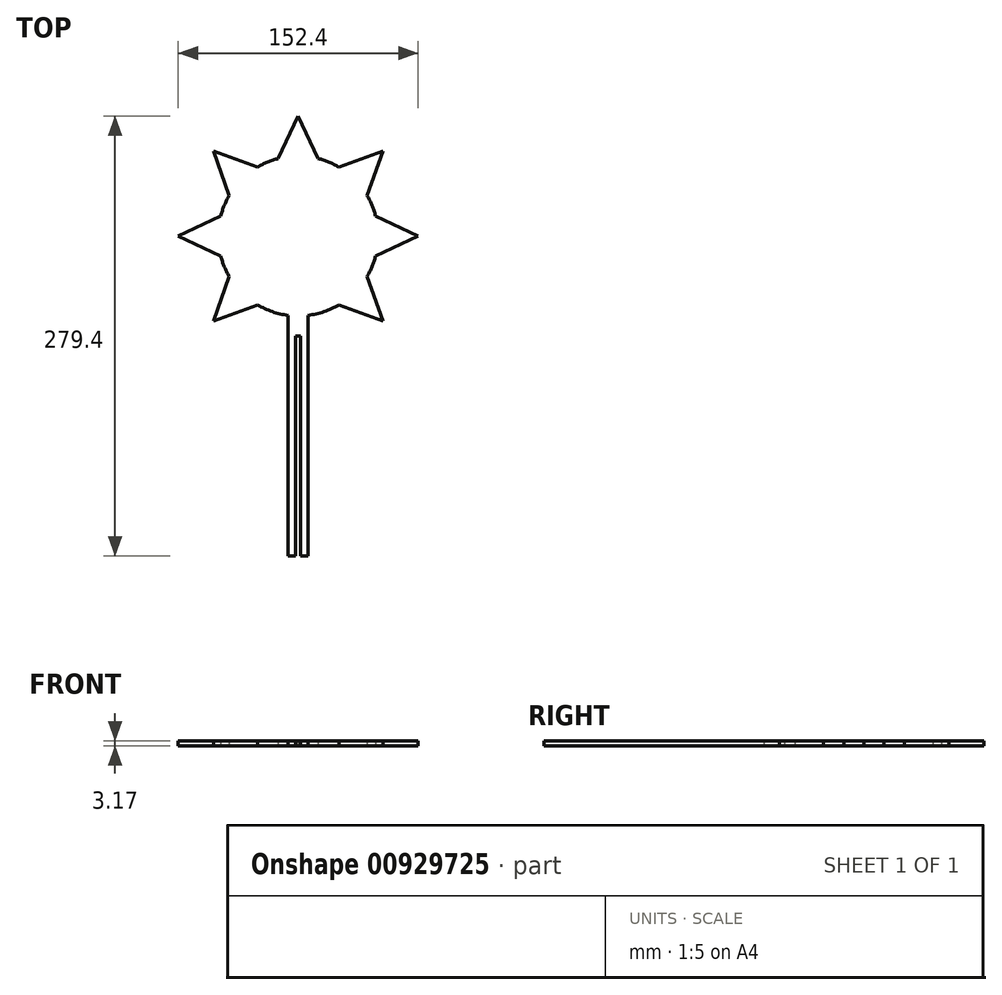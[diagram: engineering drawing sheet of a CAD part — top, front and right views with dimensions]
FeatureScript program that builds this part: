
annotation { "Feature Type Name" : "Feature", "Feature Type Description" : "" }
export const myFeature = defineFeature(function(context is Context, id is Id, definition is map)
    precondition{}
    {
        {
            var Q0;
            Q0=qCreatedBy(makeId("Top.planeOp"),FACE);
            var sketch = newSketch(context, id + "F0", { "sketchPlane" : qUnion([Q0])});
            skLineSegment(sketch, "E0.bottom", {"start": v(-6.35, -101.6) * mm, "end": v(-1.59, -101.6) * mm});
            skLineSegment(sketch, "E0.left", {"start": v(-6.35, -101.6) * mm, "end": v(-6.35, 51.2) * mm});
            skLineSegment(sketch, "E0.right", {"start": v(6.35, -101.6) * mm, "end": v(6.35, 51.2) * mm});
            skPoint(sketch, "E0.middle", {"position": v(0, 0) * mm});
            skArc(sketch, "E1", {"start": v(6.35, 51.2) * mm, "mid": v(16.41, 53.52) * mm, "end": v(25.8, 57.84) * mm});
            skLineSegment(sketch, "E2", {"start": v(-49.19, 88.9) * mm, "end": v(-76.2, 101.6) * mm});
            skLineSegment(sketch, "E3", {"start": v(-76.2, 101.6) * mm, "end": v(-49.19, 114.3) * mm});
            skLineSegment(sketch, "E4", {"start": v(49.19, 114.3) * mm, "end": v(76.2, 101.6) * mm});
            skLineSegment(sketch, "E5", {"start": v(76.2, 101.6) * mm, "end": v(49.19, 88.9) * mm});
            skLineSegment(sketch, "E6", {"start": v(12.7, 150.79) * mm, "end": v(0, 177.8) * mm});
            skLineSegment(sketch, "E7", {"start": v(0, 177.8) * mm, "end": v(-12.7, 150.79) * mm});
            skLineSegment(sketch, "E8", {"start": v(-25.8, 145.36) * mm, "end": v(-53.88, 155.48) * mm});
            skLineSegment(sketch, "E9", {"start": v(-53.88, 155.48) * mm, "end": v(-43.76, 127.4) * mm});
            skLineSegment(sketch, "E10", {"start": v(43.76, 127.4) * mm, "end": v(53.88, 155.48) * mm});
            skLineSegment(sketch, "E11", {"start": v(53.88, 155.48) * mm, "end": v(25.8, 145.36) * mm});
            skPoint(sketch, "E12.orphan", {"position": v(6.35, 101.6) * mm});
            skPoint(sketch, "E0.top.start.orphan", {"position": v(-6.35, 101.6) * mm});
            skArc(sketch, "E13.trimOffspring", {"start": v(-49.19, 88.9) * mm, "mid": v(-46.93, 82.16) * mm, "end": v(-43.76, 75.8) * mm});
            skArc(sketch, "E14.trimOffspring", {"start": v(-43.76, 127.4) * mm, "mid": v(-46.93, 121.04) * mm, "end": v(-49.19, 114.3) * mm});
            skArc(sketch, "E15.trimOffspring", {"start": v(-12.7, 150.79) * mm, "mid": v(-19.44, 148.53) * mm, "end": v(-25.8, 145.36) * mm});
            skArc(sketch, "E16.trimOffspring", {"start": v(25.8, 145.36) * mm, "mid": v(19.44, 148.53) * mm, "end": v(12.7, 150.79) * mm});
            skArc(sketch, "E17.trimOffspring", {"start": v(49.19, 114.3) * mm, "mid": v(46.93, 121.04) * mm, "end": v(43.76, 127.4) * mm});
            skLineSegment(sketch, "E18", {"start": v(-43.76, 75.8) * mm, "end": v(-53.88, 47.72) * mm});
            skLineSegment(sketch, "E19", {"start": v(-53.88, 47.72) * mm, "end": v(-25.8, 57.84) * mm});
            skLineSegment(sketch, "E20", {"start": v(43.76, 75.8) * mm, "end": v(53.88, 47.72) * mm});
            skLineSegment(sketch, "E21", {"start": v(53.88, 47.72) * mm, "end": v(25.8, 57.84) * mm});
            skArc(sketch, "E22.trimOffspring", {"start": v(-25.8, 57.84) * mm, "mid": v(-16.41, 53.52) * mm, "end": v(-6.35, 51.2) * mm});
            skArc(sketch, "E23.trimOffspring", {"start": v(43.76, 75.8) * mm, "mid": v(46.93, 82.16) * mm, "end": v(49.19, 88.9) * mm});
            skLineSegment(sketch, "E24.top", {"start": v(-1.59, 38.1) * mm, "end": v(1.59, 38.1) * mm});
            skLineSegment(sketch, "E24.left", {"start": v(-1.59, -101.6) * mm, "end": v(-1.59, 38.1) * mm});
            skLineSegment(sketch, "E24.right", {"start": v(1.59, -101.6) * mm, "end": v(1.59, 38.1) * mm});
            skLineSegment(sketch, "E25.trimOffspring", {"start": v(1.59, -101.6) * mm, "end": v(6.35, -101.6) * mm});
            skSolve(sketch);
        }
        {
            var Q0;
            Q0 = qSketchRegion(id + "F0", true);
            extrude(context, id + "F1", {"entities" : qUnion([Q0]), "depth" : 3.17 * mm, "offsetDistance" : 25.4 * mm});
        }
    });
